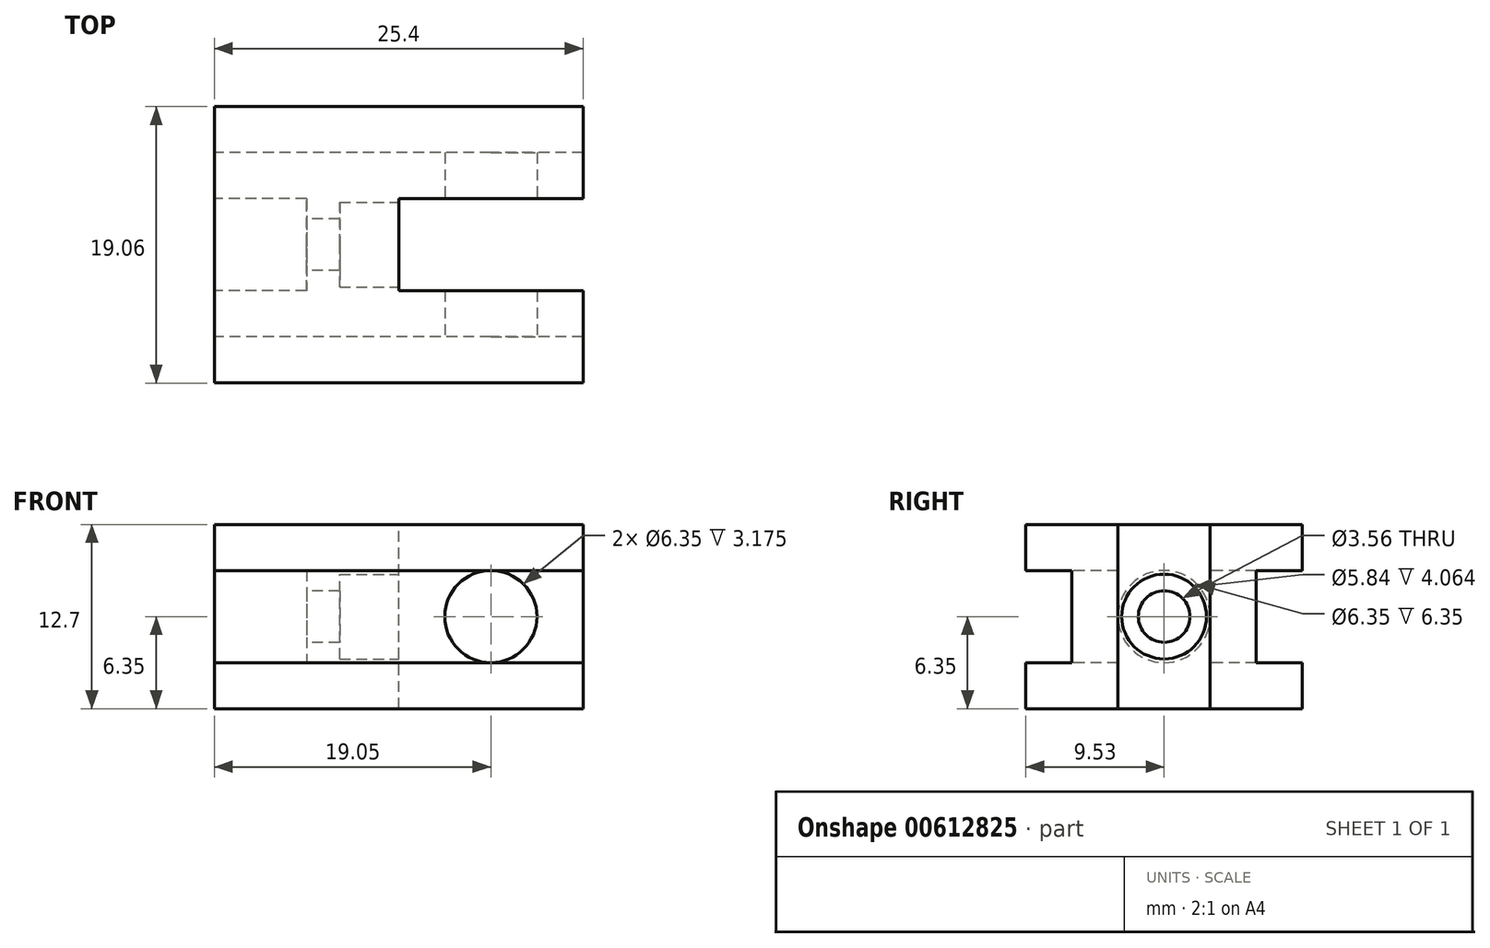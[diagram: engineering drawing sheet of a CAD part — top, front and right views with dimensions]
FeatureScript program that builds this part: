
annotation { "Feature Type Name" : "Feature", "Feature Type Description" : "" }
export const myFeature = defineFeature(function(context is Context, id is Id, definition is map)
    precondition{}
    {
        {
            var Q0;
            Q0=qCreatedBy(makeId("Right.planeOp"),FACE);
            var sketch = newSketch(context, id + "F0", { "sketchPlane" : qUnion([Q0])});
            skLineSegment(sketch, "E0", {"start": v(-6.35, -3.17) * mm, "end": v(-6.35, 3.17) * mm});
            skLineSegment(sketch, "E1", {"start": v(-6.35, 3.17) * mm, "end": v(-9.53, 3.17) * mm});
            skLineSegment(sketch, "E2", {"start": v(-9.52, 3.17) * mm, "end": v(-9.52, 6.35) * mm});
            skLineSegment(sketch, "E3", {"start": v(-9.52, 6.35) * mm, "end": v(9.52, 6.35) * mm});
            skLineSegment(sketch, "E4", {"start": v(9.53, 6.35) * mm, "end": v(9.53, 3.17) * mm});
            skLineSegment(sketch, "E5", {"start": v(9.53, 3.17) * mm, "end": v(6.35, 3.17) * mm});
            skLineSegment(sketch, "E6", {"start": v(6.35, 3.17) * mm, "end": v(6.35, -3.17) * mm});
            skLineSegment(sketch, "E7", {"start": v(6.35, -3.17) * mm, "end": v(9.53, -3.17) * mm});
            skLineSegment(sketch, "E8", {"start": v(9.52, -3.17) * mm, "end": v(9.52, -6.35) * mm});
            skLineSegment(sketch, "E9", {"start": v(9.53, -6.35) * mm, "end": v(-9.53, -6.35) * mm});
            skLineSegment(sketch, "E10", {"start": v(-9.53, -6.35) * mm, "end": v(-9.53, -3.17) * mm});
            skLineSegment(sketch, "E11", {"start": v(-9.53, -3.17) * mm, "end": v(-6.35, -3.17) * mm});
            skPoint(sketch, "E12", {"position": v(0, 6.35) * mm});
            skPoint(sketch, "E13", {"position": v(6.35, 0) * mm});
            skCircle(sketch, "E14", {"center": v(0, 0) * mm, "radius": 1.78 * mm});
            skSolve(sketch);
        }
        {
            var Q0;
            Q0=qSketchRegion(id+"F0",true);
            extrude(context, id + "F1", {"entities" : qUnion([Q0]), "depth" : 25.4 * mm, "symmetric" : true});
        }
        {
            var Q0;
            Q0=qCreatedBy(makeId("Front.planeOp"),FACE);
            var sketch = newSketch(context, id + "F2", { "sketchPlane" : qUnion([Q0])});
            skCircle(sketch, "E15", {"center": v(6.35, 0) * mm, "radius": 3.18 * mm});
            skSolve(sketch);
        }
        {
            var Q0;
            Q0=qSketchRegion(id+"F2",true);
            extrude(context, id + "F3", {"entities" : qUnion([Q0]), "operationType" : NewBodyOperationType.REMOVE, "oppositeDirection" : true, "depth" : 25.4 * mm, "symmetric" : true});
        }
        {
            var Q0;
            Q0=qCreatedBy(makeId("Top.planeOp"),FACE);
            var sketch = newSketch(context, id + "F4", { "sketchPlane" : qUnion([Q0])});
            skLineSegment(sketch, "E16.bottom", {"start": v(12.7, -3.18) * mm, "end": v(0, -3.18) * mm});
            skLineSegment(sketch, "E16.top", {"start": v(12.7, 3.18) * mm, "end": v(0, 3.18) * mm});
            skLineSegment(sketch, "E16.left", {"start": v(12.7, -3.18) * mm, "end": v(12.7, 3.18) * mm});
            skLineSegment(sketch, "E16.right", {"start": v(0, -3.18) * mm, "end": v(0, 3.18) * mm});
            skPoint(sketch, "E17", {"position": v(0, 0) * mm});
            skSolve(sketch);
        }
        {
            var Q0;
            Q0=qSketchRegion(id+"F4",true);
            extrude(context, id + "F5", {"entities" : qUnion([Q0]), "operationType" : NewBodyOperationType.REMOVE, "oppositeDirection" : true, "depth" : 25.4 * mm, "symmetric" : true});
        }
        {
            var Q0;
            Q0=makeQuery(id+"F5.boolean.opBoolean","COPY",FACE,{"derivedFrom":makeQuery(id+"F5.opExtrude","SWEPT_FACE",FACE,{"disambiguationData":[OSD([sQuery(id+"F4.wireOp",EDGE,"E16.right")])]})});
            var sketch = newSketch(context, id + "F6", { "sketchPlane" : qUnion([Q0])});
            skCircle(sketch, "E18", {"center": v(0, 0) * mm, "radius": 2.92 * mm});
            skSolve(sketch);
        }
        {
            var Q0;
            Q0=qSketchRegion(id+"F6",true);
            extrude(context, id + "F7", {"entities" : qUnion([Q0]), "operationType" : NewBodyOperationType.REMOVE, "oppositeDirection" : true, "depth" : 4.06 * mm});
        }
        {
            var Q0;
            Q0=makeQuery(id+"F1.opExtrude","CAP_FACE",FACE,{"disambiguationData":[OSD([sQuery(id+"F0.wireOp",EDGE,"E0"),sQuery(id+"F0.wireOp",EDGE,"E1"),sQuery(id+"F0.wireOp",EDGE,"E2"),sQuery(id+"F0.wireOp",EDGE,"E3"),sQuery(id+"F0.wireOp",EDGE,"E4"),sQuery(id+"F0.wireOp",EDGE,"E5"),sQuery(id+"F0.wireOp",EDGE,"E6"),sQuery(id+"F0.wireOp",EDGE,"E7"),sQuery(id+"F0.wireOp",EDGE,"E8"),sQuery(id+"F0.wireOp",EDGE,"E9"),sQuery(id+"F0.wireOp",EDGE,"E10"),sQuery(id+"F0.wireOp",EDGE,"E11"),sQuery(id+"F0.wireOp",EDGE,"E14")])],"isStart":true});
            var sketch = newSketch(context, id + "F8", { "sketchPlane" : qUnion([Q0])});
            skCircle(sketch, "E19", {"center": v(0, 0) * mm, "radius": 3.18 * mm});
            skSolve(sketch);
        }
        {
            var Q0;
            Q0=qSketchRegion(id+"F8",true);
            extrude(context, id + "F9", {"entities" : qUnion([Q0]), "operationType" : NewBodyOperationType.REMOVE, "oppositeDirection" : true, "depth" : 6.35 * mm});
        }
    });
